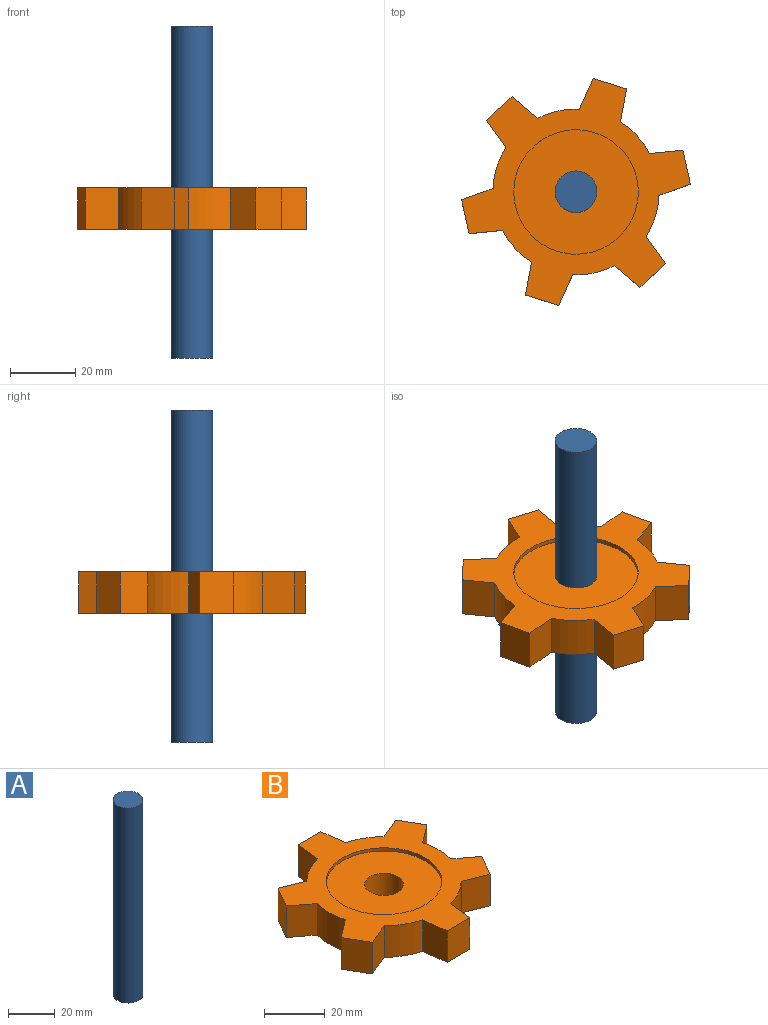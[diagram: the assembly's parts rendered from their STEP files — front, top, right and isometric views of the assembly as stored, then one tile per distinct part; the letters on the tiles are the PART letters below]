
ASSEMBLY  parts=2 mates=2
PART A: 3 faces, bbox 12.7x12.7x101.6 mm
  f0: cylinder r=6.35mm len=101.6mm, axis (0,0,-1), area 4053.7mm2, adj f1,f2
  f1: plane 12.7x12.7mm, normal (0,0,1), area 126.7mm2, adj f0
  f2: plane 12.7x12.7mm, normal (0,0,-1), area 126.7mm2, adj f0
PART B: 31 faces, bbox 65.4x69.4x12.7 mm
  f0: cylinder r=25.4mm len=12.7mm, axis (0,0,-1), area 168.9mm2, adj f6,f7,f10,f24
  f1: cylinder r=25.4mm len=13.15mm, axis (0,0,-1), area 168.9mm2, adj f6,f7,f13,f25
  f2: cylinder r=25.4mm len=12.7mm, axis (0,0,-1), area 168.9mm2, adj f6,f7,f12,f16
  f3: cylinder r=25.4mm len=12.7mm, axis (0,0,-1), area 168.9mm2, adj f6,f7,f15,f19
  f4: cylinder r=25.4mm len=13.15mm, axis (0,0,-1), area 168.9mm2, adj f6,f7,f18,f21
  f5: cylinder r=25.4mm len=12.7mm, axis (0,0,-1), area 168.9mm2, adj f6,f7,f9,f22
  f6: plane 69.39x65.4mm, normal (0,0,1), area 1565.1mm2, adj f0,f1,f2,f3,f4,f5,f8,f9
  f7: plane 69.39x65.4mm, normal (0,0,-1), area 1565.1mm2, adj f0,f1,f2,f3,f4,f5,f8,f9
  f8: plane 12.7x10.61mm, normal (0,1,0), area 134.7mm2, adj f6,f7,f9,f10
  f9: plane 12.7x10.16mm, normal (-0.99,0.12,0), area 130mm2, adj f5,f6,f7,f8
  f10: plane 12.7x10.16mm, normal (0.99,0.12,0), area 130mm2, adj f0,f6,f7,f8
  f11: plane 12.7x9.19mm, normal (0.87,-0.5,0), area 134.7mm2, adj f6,f7,f12,f13
  f12: plane 12.7x9.43mm, normal (-0.39,-0.92,0), area 130mm2, adj f2,f6,f7,f11
  f13: plane 12.7x8.16mm, normal (0.6,0.8,0), area 130mm2, adj f1,f6,f7,f11
  f14: plane 12.7x10.61mm, normal (0,-1,0), area 134.7mm2, adj f6,f7,f15,f16
  f15: plane 12.7x10.16mm, normal (-0.99,-0.12,0), area 130mm2, adj f3,f6,f7,f14
  f16: plane 12.7x10.16mm, normal (0.99,-0.12,0), area 130mm2, adj f2,f6,f7,f14
  f17: plane 12.7x9.19mm, normal (-0.87,-0.5,0), area 134.7mm2, adj f6,f7,f18,f19
  f18: plane 12.7x8.16mm, normal (-0.6,0.8,0), area 130mm2, adj f4,f6,f7,f17
  f19: plane 12.7x9.43mm, normal (0.39,-0.92,0), area 130mm2, adj f3,f6,f7,f17
  f20: plane 12.7x9.19mm, normal (-0.87,0.5,0), area 134.7mm2, adj f6,f7,f21,f22
  f21: plane 12.7x8.16mm, normal (-0.6,-0.8,0), area 130mm2, adj f4,f6,f7,f20
  f22: plane 12.7x9.43mm, normal (0.39,0.92,0), area 130mm2, adj f5,f6,f7,f20
  f23: plane 12.7x9.19mm, normal (0.87,0.5,0), area 134.7mm2, adj f6,f7,f24,f25
  f24: plane 12.7x9.43mm, normal (-0.39,0.92,0), area 130mm2, adj f0,f6,f7,f23
  f25: plane 12.7x8.16mm, normal (0.6,-0.8,0), area 130mm2, adj f1,f6,f7,f23
  f26: cylinder r=19.05mm len=38.1mm, axis (0,0,1), area 152mm2, adj f6,f27
  f27: plane 38.1x38.1mm, normal (0,0,1), area 1013.4mm2, adj f26,f30
  f28: cylinder r=19.05mm len=38.1mm, axis (0,0,-1), area 152mm2, adj f7,f29
  f29: plane 38.1x38.1mm, normal (0,0,-1), area 1013.4mm2, adj f28,f30
  f30: cylinder r=6.35mm len=12.7mm, axis (0,0,1), area 405.4mm2, adj f27,f29
PLACE A t=(-58.04,-33.04,32.56)mm fixed
PLACE B rot(axis=(0,0,-1),137.4deg) t=(-58.04,-33.04,27.48)mm
MATE planar A.f0 <-> B.f0  axis (0,0,1) through (-58.04,-33.04,83.36)mm
MATE cylindrical A.f0 <-> B.f0  axis (0,0,-1) through (-58.04,-33.04,32.56)mm
